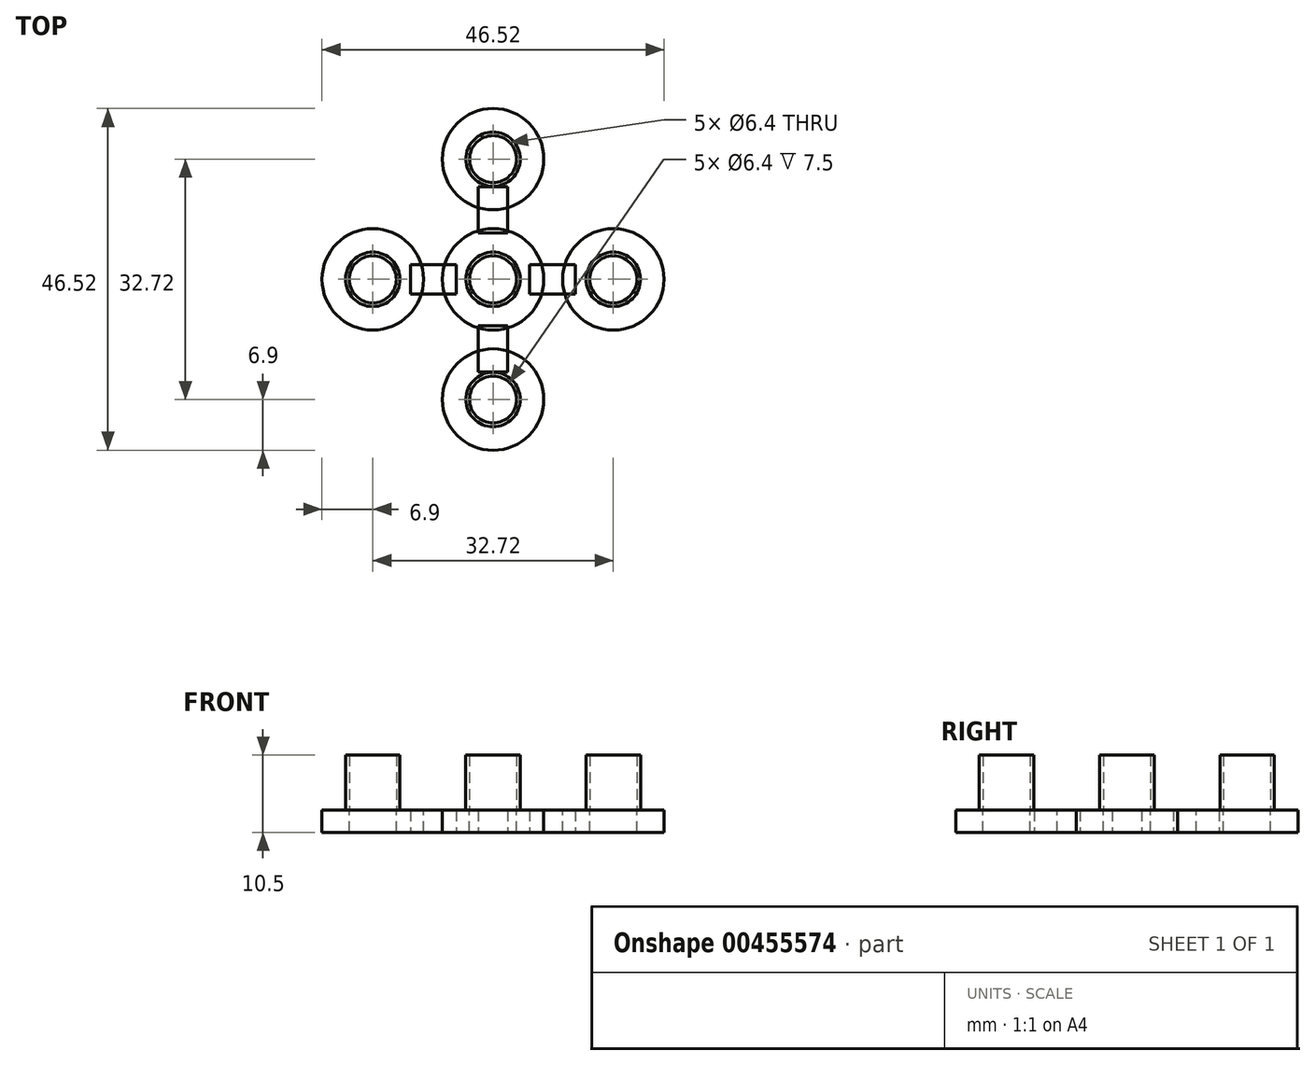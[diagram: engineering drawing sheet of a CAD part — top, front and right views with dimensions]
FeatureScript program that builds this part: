
annotation { "Feature Type Name" : "Feature", "Feature Type Description" : "" }
export const myFeature = defineFeature(function(context is Context, id is Id, definition is map)
    precondition{}
    {
        {
            var Q0;
            Q0=qCreatedBy(makeId("Top.planeOp"),FACE);
            var sketch = newSketch(context, id + "F0", { "sketchPlane" : qUnion([Q0])});
            skCircle(sketch, "E0", {"center": v(0, 0) * mm, "radius": 3.7 * mm});
            skCircle(sketch, "E1", {"center": v(0, 16.36) * mm, "radius": 3.7 * mm});
            skCircle(sketch, "E2.MirrorC", {"center": v(0, -16.36) * mm, "radius": 3.7 * mm});
            skCircle(sketch, "E3", {"center": v(16.36, 0) * mm, "radius": 3.7 * mm});
            skCircle(sketch, "E4.MirrorC", {"center": v(-16.36, 0) * mm, "radius": 3.7 * mm});
            skCircle(sketch, "E5", {"center": v(0, 16.36) * mm, "radius": 3.2 * mm});
            skCircle(sketch, "E6", {"center": v(16.36, 0) * mm, "radius": 3.2 * mm});
            skCircle(sketch, "E7", {"center": v(0, 0) * mm, "radius": 3.2 * mm});
            skCircle(sketch, "E8.MirrorC", {"center": v(0, -16.36) * mm, "radius": 3.2 * mm});
            skCircle(sketch, "E9.MirrorC", {"center": v(-16.36, 0) * mm, "radius": 3.2 * mm});
            skSolve(sketch);
        }
        {
            var Q0;
            Q0 = qSketchRegion(id + "F0", true);
            extrude(context, id + "F1", {"entities" : qUnion([Q0]), "depth" : 7.5 * mm});
        }
        {
            var Q0;
            Q0=qCreatedBy(makeId("Top.planeOp"),FACE);
            var sketch = newSketch(context, id + "F2", { "sketchPlane" : qUnion([Q0])});
            skCircle(sketch, "E10", {"center": v(0, 0) * mm, "radius": 6.9 * mm});
            skCircle(sketch, "E11", {"center": v(16.36, 0) * mm, "radius": 6.9 * mm});
            skCircle(sketch, "E12", {"center": v(0, 16.36) * mm, "radius": 6.9 * mm});
            skCircle(sketch, "E13.MirrorC", {"center": v(0, -16.36) * mm, "radius": 6.9 * mm});
            skCircle(sketch, "E14.MirrorC", {"center": v(-16.36, 0) * mm, "radius": 6.9 * mm});
            skCircle(sketch, "E15", {"center": v(0, 0) * mm, "radius": 3.2 * mm});
            skCircle(sketch, "E16", {"center": v(0, 16.36) * mm, "radius": 3.2 * mm});
            skCircle(sketch, "E17", {"center": v(16.36, 0) * mm, "radius": 3.2 * mm});
            skCircle(sketch, "E18", {"center": v(0, -16.36) * mm, "radius": 3.2 * mm});
            skCircle(sketch, "E19", {"center": v(-16.36, 0) * mm, "radius": 3.2 * mm});
            skSolve(sketch);
        }
        {
            var Q0;
            Q0 = qSketchRegion(id + "F2", true);
            extrude(context, id + "F3", {"entities" : qUnion([Q0]), "oppositeDirection" : true, "depth" : 3 * mm});
        }
        {
            var Q0;
            Q0=makeQuery(id+"F3.opExtrude","CAP_FACE",FACE,{"disambiguationData":[OSD([sQuery(id+"F2.wireOp",EDGE,"E13.MirrorC"),sQuery(id+"F2.wireOp",EDGE,"E18")])],"isStart":false});
            var sketch = newSketch(context, id + "F4", { "sketchPlane" : qUnion([Q0])});
            skLineSegment(sketch, "E20.bottom", {"start": v(2, 12.58) * mm, "end": v(-2, 12.58) * mm});
            skLineSegment(sketch, "E20.top", {"start": v(2, 6.34) * mm, "end": v(-2, 6.34) * mm});
            skLineSegment(sketch, "E20.left", {"start": v(2, 6.34) * mm, "end": v(2, 12.58) * mm});
            skLineSegment(sketch, "E20.right", {"start": v(-2, 6.34) * mm, "end": v(-2, 12.58) * mm});
            skPoint(sketch, "E20.middle", {"position": v(0, 9.46) * mm});
            skLineSegment(sketch, "E21.MirrorCS", {"start": v(2, -6.34) * mm, "end": v(2, -12.58) * mm});
            skLineSegment(sketch, "E22.MirrorCS", {"start": v(2, -6.34) * mm, "end": v(-2, -6.34) * mm});
            skLineSegment(sketch, "E23.MirrorCS", {"start": v(-2, -6.34) * mm, "end": v(-2, -12.58) * mm});
            skLineSegment(sketch, "E24.MirrorCS", {"start": v(2, -12.58) * mm, "end": v(-2, -12.58) * mm});
            skLineSegment(sketch, "E25.bottom", {"start": v(-11.21, -2) * mm, "end": v(-4.98, -2) * mm});
            skLineSegment(sketch, "E25.top", {"start": v(-11.21, 2) * mm, "end": v(-4.98, 2) * mm});
            skLineSegment(sketch, "E25.left", {"start": v(-11.21, -2) * mm, "end": v(-11.21, 2) * mm});
            skLineSegment(sketch, "E25.right", {"start": v(-4.98, -2) * mm, "end": v(-4.98, 2) * mm});
            skPoint(sketch, "E25.middle", {"position": v(-8.1, 0) * mm});
            skPoint(sketch, "E26.MirrorP", {"position": v(8.1, 0) * mm});
            skLineSegment(sketch, "E27.MirrorCS", {"start": v(11.21, -2) * mm, "end": v(4.98, -2) * mm});
            skLineSegment(sketch, "E28.MirrorCS", {"start": v(11.21, 2) * mm, "end": v(4.98, 2) * mm});
            skLineSegment(sketch, "E29.MirrorCS", {"start": v(4.98, -2) * mm, "end": v(4.98, 2) * mm});
            skLineSegment(sketch, "E30.MirrorCS", {"start": v(11.21, -2) * mm, "end": v(11.21, 2) * mm});
            skSolve(sketch);
        }
        {
            var Q0;
            Q0 = qSketchRegion(id + "F4", true);
            extrude(context, id + "F5", {"entities" : qUnion([Q0]), "oppositeDirection" : true, "depth" : 3 * mm});
        }
    });
